# Revit family: PRD_AR_SoapDpnsrs_EXOSSoapDispenser_EXOS616,618,625,X-B-W
name_source: partatom
category: Specialty Equipment
revit_build: Autodesk Revit 2018 (Build: 20190510_1515(x64)
units: mm (PartAtom-declared; Revit-internal decimal feet)

## family parameters
Cut with Voids When Loaded = No
Host = Face
OmniClass Number = 23.40.20.21.34
OmniClass Title = Soap Holders, Dispensers
Part Type = Normal
Room Calculation Point = No
Round Connector Dimension = Use Diameter
Shared = No

## types (9) — shared parameters
AssetType = Fixed
Category = Pr_40_70_22_81, Soap dispensers
Color = Stainless steel
Default Elevation = 1050 mm
DurationUnit = year
Features = stainless steel, 1.20 mm, satin finished, wall mounting
Finish = Satin finished
Form = Wall mounted
IfcExportAs = IfcFurnitureType
IfcExportType = NOTDEFINED
Lock = key-lock
MainColor = Stainless steel
Manufacturer = KWC Group AG
ManufacturerName = KWC Group AG
ManufacturerURL = www.kwc.com
Material = Stainless steel
MaterialCode = Stainless steel 1.4301
NBSDescription = Soap dispensers
NBSReference = 45-35-72/358
NominalDepth = 120 mm  [stored 0.393701 ft]
NominalLength = 120 mm  [stored 0.393701 ft]
NominalWidth = 120 mm  [stored 0.393701 ft]
Operation = Manual
ProductInformation = https://pim.kwc.com
SoapDispenserMaterial = PRD_AR_StainlessSteel_SatinFinished
Style = Soap dispenser
SurfaceTreatment = InoxPlus (anti fingerprint)
TypeOfMounting = Wall mounting
URL = www.kwc.com
Uniclass2015Code = Pr_40_70_22_81
Uniclass2015Title = Soap dispensers
Uniclass2015Version = Products v1.10
Version = 1
WarrantyDurationUnit = year

## per-type parameters (varying)
| type | BIMObjectName | Description | FillingQuantity | GrossWeight | IntegralAccessories | ModelNumber | Name | NetWeight | NominalHeight | NumberOfBatteries | PanelMaterial | PullLeverEXOS616 | PullLeverEXOS618 | Size | TypeOfBatteries | TypeOfConsumable | TypeOfOperation | TypeOfSoapContainer |
| EXOS618B | PRD_AR_SpDpnsrs_EXOSSoapDispenser_EXOS618B | Soap dispenser for wall mounting, stainless steel with satin finish, black safety glass front panel, casing with InoxPlus surface refinement for the reduction of finger marks and better cleaning characteristics (easy to clean), material thickness 1.2 mm, inspection window on side, suitable for liquid soap and lotions, 800 ml refill tank, with stainless steel push lever, easy to refill with soap tank on front panel, includes mounting materials.Dimensions: 120 x 345 x 120 mm (W x H x D) | 800 ml | 2.77 kg | Incl. mounting materials | 2030022940 | Foam soap dispenser EXOS618B | 2.41 kg | 345 mm  [stored 1.13189 ft] |  | PRD_AR_Glass_Black | No | Yes | 120x345x120 mm |  | Liquid soap | Manual operation | Integrated refillable tank |
| EXOS618X | PRD_AR_SpDpnsrs_EXOSSoapDispenser_EXOS618X | Soap dispenser for wall mounting, stainless steel with satin finish, front and casing with InoxPlus surface refinement for the reduction of finger marks and better cleaning characteristics (easy to clean), material thickness 1.2 mm, inspection window on side, suitable for liquid soap and lotions, 800 ml refill tank, with stainless steel push lever, easy to refill with soap tank on front panel, includes mounting materials. | 800 ml | 2.62 kg | Incl. mounting materials | 2030022939 | Foam soap dispenser EXOS618X | 2.17 kg | 345 mm  [stored 1.13189 ft] |  | PRD_AR_StainlessSteel_SatinFinished | No | Yes | 120x345x120 mm |  | Liquid soap | Manual operation | Integrated refillable tank |
| EXOS618W | PRD_AR_SpDpnsrs_EXOSSoapDispenser_EXOS618W | Soap dispenser for wall mounting, stainless steel with satin finish, white safety glass front panel, casing with InoxPlus surface refinement for the reduction of finger marks and better cleaning characteristics (easy to clean), material thickness 1.2 mm, inspection window on side, suitable for liquid soap and lotions, 800 ml refill tank, with stainless steel push lever, easy to refill with soap tank on front panel, includes mounting materials. | 800 ml | 2.78 kg | Incl. mounting materials | 2030025230 | Foam soap dispenser EXOS618W | 2.34 kg | 345 mm  [stored 1.13189 ft] |  | PRD_AR_Glass_White | No | Yes | 120x345x120 mm |  | Liquid soap | Manual operation | Integrated refillable tank |
| EXOS616B | PRD_AR_SpDpnsrs_EXOSSoapDispenser_EXOS616B | Foam soap dispenser for wall mounting, stainless steel with satin finish, black safety glass front panel, casing with InoxPlus surface refinement for the reduction of finger marks and better cleaning characteristics (easy to clean), material thickness 1.2 mm, inspection window on side, with stainless steel pull lever, suitable for KWC foam soap, includes mounting materials and 650 ml KWC foam soap. | 650 ml | 3.54 kg | Incl. mounting materials and 650 ml Franke foam soap | 2030022946 | Foam soap dispenser EXOS616B | 3.18 kg | 358 mm  [stored 1.17454 ft] |  | PRD_AR_Glass_Black | Yes | No | 120x358x120 mm |  | Foam soap | Manual operation | Single-use bag |
| EXOS616W | PRD_AR_SpDpnsrs_EXOSSoapDispenser_EXOS616W | Foam soap dispenser for wall mounting, stainless steel with satin finish, white safety glass front panel, casing with InoxPlus surface refinement for the reduction of finger marks and better cleaning characteristics (easy to clean), material thickness 1.2 mm, inspection window on side, with stainless steel pull lever, suitable for KWC foam soap, includes mounting materials and 650 ml KWC foam soap. | 650 ml | 3.52 kg | Incl. mounting materials and 650 ml Franke foam soap | 2030025232 | Foam soap dispenser EXOS616W | 3.15 kg | 358 mm  [stored 1.17454 ft] |  | PRD_AR_Glass_White | Yes | No | 120x358x120 mm |  | Foam soap | Manual operation | Single-use bag |
| EXOS616X | PRD_AR_SpDpnsrs_EXOSSoapDispenser_EXOS616X | Foam soap dispenser for wall mounting, stainless steel with satin finish, front and casing with InoxPlus surface refinement for the reduction of finger marks and better cleaning characteristics (easy to clean), material thickness 1.2 mm, inspection window on side, with stainless steel pull lever, suitable for KWC foam soap, includes mounting materials and 650 ml KWC foam soap. | 650 ml | 3.28 kg | Incl. mounting materials and 650 ml Franke foam soap | 2030022945 | Foam soap dispenser EXOS616X | 2.92 kg | 358 mm  [stored 1.17454 ft] |  | PRD_AR_StainlessSteel_SatinFinished | Yes | No | 120x358x120 mm |  | Foam soap | Manual operation | Single-use bag |
| EXOS625X | PRD_AR_SpDpnsrs_EXOSSoapDispenser_EXOS625X | Touch free soap dispenser for wall mounting, stainless steel with satin finish, front and casing with InoxPlus surface refinement for the reduction of finger marks and better cleaning characteristics (easy to clean), material thickness 1.2 mm, inspection window on side, infrared sensor activity for non-touch operation, LED display shows battery status, requires 4 pieces 1.5V AA batteries, suitable for liquid soap and lotions, includes 800 ml refill tank, dispenses 0.6 - 1.1 ml depending on soap, includes mounting materials. | 800 ml | 2.54 kg | Incl. mounting materials | 2030022942 | Foam soap dispenser EXOS625X | 2.43 kg | 325 mm  [stored 1.06627 ft] | 4 | PRD_AR_StainlessSteel_SatinFinished | No | No | 120x325x120 mm | AA Mignon battery 1.5 V | Liquid soap | Sensor operation | Integrated refillable tank |
| EXOS625B | PRD_AR_SpDpnsrs_EXOSSoapDispenser_EXOS625B | Touch free soap dispenser for wall mounting, stainless steel with satin finish, black safety glass front panel, casing with InoxPlus surface refinement for the reduction of finger marks and better cleaning characteristics (easy to clean), material thickness 1.2 mm, inspection window on side, infrared sensor activity for non-touch operation, LED display shows battery status, requires 4 pieces 1.5V AA batteries, suitable for liquid soap and lotions, includes 800 ml refill tank, dispenses 0.6 - 1.1 ml depending on soap, includes mounting materials. | 800 ml | 2.84 kg | Incl. mounting materials | 2030022943 | Foam soap dispenser EXOS625B | 2.75 kg | 325 mm  [stored 1.06627 ft] | 4 | PRD_AR_Glass_Black | No | No | 120x325x120 mm | AA Mignon battery 1.5 V | Liquid soap | Sensor operation | Integrated refillable tank |
| EXOS625W | PRD_AR_SpDpnsrs_EXOSSoapDispenser_EXOS625W | Touch free soap dispenser for wall mounting, stainless steel with satin finish, white safety glass front panel, casing with InoxPlus surface refinement for the reduction of finger marks and better cleaning characteristics (easy to clean), material thickness 1.2 mm, inspection window on side, infrared sensor activity for non-touch operation, LED display shows battery status, requires 4 pieces 1.5V AA batteries, suitable for liquid soap and lotions, includes 800 ml refill tank, dispenses 0.6 - 1.1 ml depending on soap, includes mounting materials. | 800 ml | 2.78 kg | Incl. mounting materials | 2030025231 | Foam soap dispenser EXOS625W | 2.68 kg | 325 mm  [stored 1.06627 ft] | 4 | PRD_AR_Glass_White | No | No | 120x325x120 mm | AA Mignon battery 1.5 V | Liquid soap | Sensor operation | Integrated refillable tank |

note: column(s) folded — value = type name in every type: Model, ModelReference

note: [stored X ft] marks values corroborated as IEEE doubles in the binary element streams (Revit-internal decimal feet)

## geometry (parser evidence)
native form markers: Sweep x1
no freeform markers — native parametric forms only
